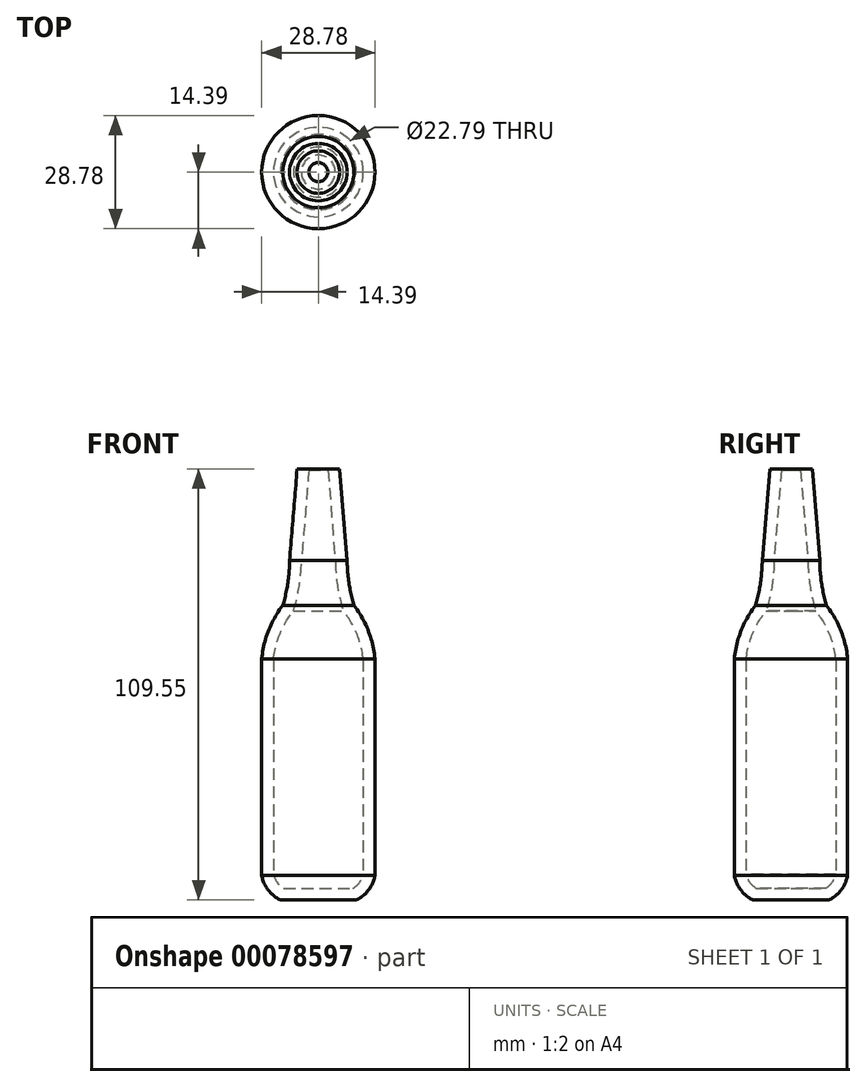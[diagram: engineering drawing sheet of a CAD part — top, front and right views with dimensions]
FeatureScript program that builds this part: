
annotation { "Feature Type Name" : "Feature", "Feature Type Description" : "" }
export const myFeature = defineFeature(function(context is Context, id is Id, definition is map)
    precondition{}
    {
        {
            var Q0;
            Q0=qCreatedBy(makeId("Front.planeOp"),FACE);
            var sketch = newSketch(context, id + "F0", { "sketchPlane" : qUnion([Q0])});
            skLineSegment(sketch, "E0", {"start": v(0, 4.04) * mm, "end": v(-9.62, 4.04) * mm});
            skArc(sketch, "E1", {"start": v(-14.4, 10.28) * mm, "mid": v(-12.76, 6.6) * mm, "end": v(-9.62, 4.04) * mm});
            skLineSegment(sketch, "E2", {"start": v(-14.4, 10.28) * mm, "end": v(-14.4, 65.28) * mm});
            skArc(sketch, "E3", {"start": v(-9.05, 78.85) * mm, "mid": v(-12.7, 72.45) * mm, "end": v(-14.4, 65.28) * mm});
            skArc(sketch, "E4", {"start": v(-9.05, 78.85) * mm, "mid": v(-7.77, 84.52) * mm, "end": v(-7.3, 90.3) * mm});
            skLineSegment(sketch, "E5", {"start": v(-7.3, 90.3) * mm, "end": v(-5.4, 113.6) * mm});
            skLineSegment(sketch, "E6.0", {"start": v(-4.3, 90.17) * mm, "end": v(-2.41, 113.35) * mm});
            skArc(sketch, "E6.1", {"start": v(-6.36, 77.42) * mm, "mid": v(-4.86, 83.72) * mm, "end": v(-4.3, 90.17) * mm});
            skLineSegment(sketch, "E6.2", {"start": v(0, 7.04) * mm, "end": v(-8.86, 7.04) * mm});
            skArc(sketch, "E6.3", {"start": v(-11.4, 10.59) * mm, "mid": v(-10.48, 8.56) * mm, "end": v(-8.86, 7.04) * mm});
            skLineSegment(sketch, "E6.4", {"start": v(-11.4, 10.59) * mm, "end": v(-11.4, 65.14) * mm});
            skArc(sketch, "E6.5", {"start": v(-6.36, 77.42) * mm, "mid": v(-9.78, 71.65) * mm, "end": v(-11.4, 65.14) * mm});
            skLineSegment(sketch, "E7", {"start": v(0, 0) * mm, "end": v(0, 139.67) * mm, "construction": true});
            skLineSegment(sketch, "E8", {"start": v(0, 7.04) * mm, "end": v(0, 4.04) * mm});
            skLineSegment(sketch, "E9", {"start": v(-2.41, 113.35) * mm, "end": v(-5.4, 113.6) * mm});
            skSolve(sketch);
        }
        {
            var Q0;
            Q0=makeQuery(id+"F0.imprint","IMPRINT",FACE,{"disambiguationData":[TD([[makeQuery(id+"F0.imprint","IMPRINT",EDGE,{"derivedFrom":sQuery(id+"F0.wireOp",EDGE,"E0")}),-1.0]])]});
            var Q1;
            Q1=sQuery(id+"F0.wireOp",EDGE,"E7");
            revolve(context, id + "F1", {"entities" : qUnion([Q0]), "axis" : qUnion([Q1]), "revolveType" : RevolveType.FULL});
        }
    });
